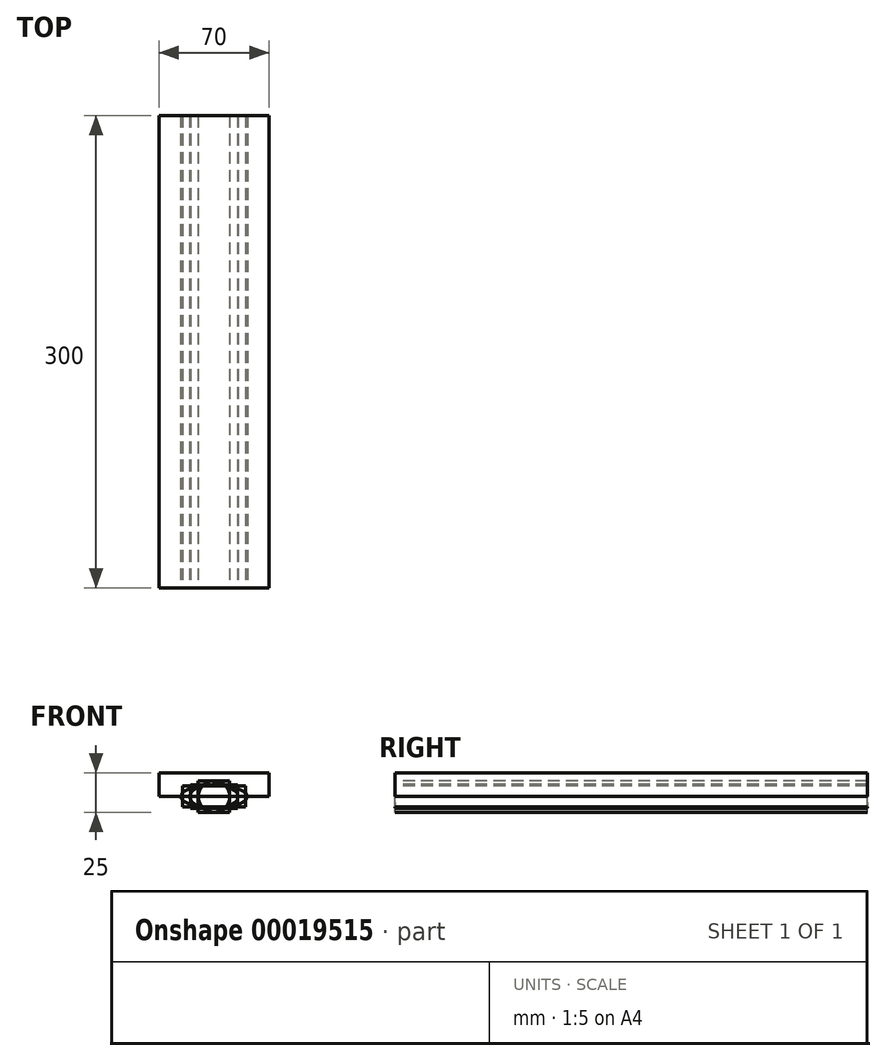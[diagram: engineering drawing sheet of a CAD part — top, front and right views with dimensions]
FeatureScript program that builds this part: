
annotation { "Feature Type Name" : "Feature", "Feature Type Description" : "" }
export const myFeature = defineFeature(function(context is Context, id is Id, definition is map)
    precondition{}
    {
        {
            var Q0;
            Q0=qCreatedBy(makeId("Front.planeOp"),FACE);
            var sketch = newSketch(context, id + "F0", { "sketchPlane" : qUnion([Q0])});
            skCircle(sketch, "E0", {"center": v(0, 0) * mm, "radius": 10 * mm});
            skSolve(sketch);
        }
        {
            var Q0;
            Q0=makeQuery(id+"F0.imprint","IMPRINT",FACE,{"disambiguationData":[TD([[makeQuery(id+"F0.imprint","IMPRINT",EDGE,{"derivedFrom":sQuery(id+"F0.wireOp",EDGE,"E0")}),1.0]])]});
            extrude(context, id + "F1", {"entities" : qUnion([Q0]), "oppositeDirection" : true, "depth" : (15 * 20) * mm});
        }
        {
            var Q0;
            Q0=qCreatedBy(makeId("Front.planeOp"),FACE);
            var sketch = newSketch(context, id + "F2", { "sketchPlane" : qUnion([Q0])});
            skLineSegment(sketch, "E1.bottom", {"start": v(10, 10) * mm, "end": v(-10, 10) * mm});
            skLineSegment(sketch, "E1.top", {"start": v(10, -10) * mm, "end": v(-10, -10) * mm});
            skLineSegment(sketch, "E1.left", {"start": v(10, 10) * mm, "end": v(10, -10) * mm});
            skLineSegment(sketch, "E1.right", {"start": v(-10, 10) * mm, "end": v(-10, -10) * mm});
            skPoint(sketch, "E1.middle", {"position": v(0, 0) * mm});
            skSolve(sketch);
        }
        {
            var Q0;
            Q0=makeQuery(id+"F2.imprint","IMPRINT",FACE,{"disambiguationData":[TD([[makeQuery(id+"F2.imprint","IMPRINT",EDGE,{"derivedFrom":sQuery(id+"F2.wireOp",EDGE,"E1.bottom")}),1.0]])]});
            extrude(context, id + "F3", {"entities" : qUnion([Q0]), "oppositeDirection" : true, "depth" : (15 * 20) * mm});
        }
        {
            var Q0;
            Q0=qCreatedBy(makeId("Front.planeOp"),FACE);
            var sketch = newSketch(context, id + "F4", { "sketchPlane" : qUnion([Q0])});
            skLineSegment(sketch, "E2.bottom", {"start": v(15, 7.5) * mm, "end": v(-15, 7.5) * mm});
            skLineSegment(sketch, "E2.top", {"start": v(15, -7.5) * mm, "end": v(-15, -7.5) * mm});
            skLineSegment(sketch, "E2.left", {"start": v(15, 7.5) * mm, "end": v(15, -7.5) * mm});
            skLineSegment(sketch, "E2.right", {"start": v(-15, 7.5) * mm, "end": v(-15, -7.5) * mm});
            skPoint(sketch, "E2.middle", {"position": v(0, 0) * mm});
            skSolve(sketch);
        }
        {
            var Q0;
            Q0=makeQuery(id+"F4.imprint","IMPRINT",FACE,{"disambiguationData":[TD([[makeQuery(id+"F4.imprint","IMPRINT",EDGE,{"derivedFrom":sQuery(id+"F4.wireOp",EDGE,"E2.bottom")}),1.0]])]});
            extrude(context, id + "F5", {"entities" : qUnion([Q0]), "oppositeDirection" : true, "depth" : (20 * 15) * mm});
        }
        {
            var Q0;
            Q0=qCreatedBy(makeId("Front.planeOp"),FACE);
            var sketch = newSketch(context, id + "F6", { "sketchPlane" : qUnion([Q0])});
            skEllipse(sketch, "E3", {"center": v(0, 0) * mm, "majorRadius": 15.42 * mm, "minorRadius": 7.7 * mm, "majorAxis": v(1, 0)});
            skSolve(sketch);
        }
        {
            var Q0;
            Q0=makeQuery(id+"F6.imprint","IMPRINT",FACE,{"disambiguationData":[TD([[makeQuery(id+"F6.imprint","IMPRINT",EDGE,{"derivedFrom":sQuery(id+"F6.wireOp",EDGE,"E3")}),1.0]])]});
            extrude(context, id + "F7", {"entities" : qUnion([Q0]), "oppositeDirection" : true, "depth" : (20 * 15) * mm});
        }
        {
            var Q0;
            Q0=qCreatedBy(makeId("Front.planeOp"),FACE);
            var sketch = newSketch(context, id + "F8", { "sketchPlane" : qUnion([Q0])});
            skLineSegment(sketch, "E4.bottom", {"start": v(20, 6.67) * mm, "end": v(-20, 6.67) * mm});
            skLineSegment(sketch, "E4.top", {"start": v(20, -6.67) * mm, "end": v(-20, -6.67) * mm});
            skLineSegment(sketch, "E4.left", {"start": v(20, 6.67) * mm, "end": v(20, -6.67) * mm});
            skLineSegment(sketch, "E4.right", {"start": v(-20, 6.67) * mm, "end": v(-20, -6.67) * mm});
            skPoint(sketch, "E4.middle", {"position": v(0, 0) * mm});
            skSolve(sketch);
        }
        {
            var Q0;
            Q0=makeQuery(id+"F8.imprint","IMPRINT",FACE,{"disambiguationData":[TD([[makeQuery(id+"F8.imprint","IMPRINT",EDGE,{"derivedFrom":sQuery(id+"F8.wireOp",EDGE,"E4.bottom")}),1.0]])]});
            extrude(context, id + "F9", {"entities" : qUnion([Q0]), "oppositeDirection" : true, "depth" : (20 * 15) * mm});
        }
        {
            var Q0;
            Q0=qCreatedBy(makeId("Front.planeOp"),FACE);
            var sketch = newSketch(context, id + "F10", { "sketchPlane" : qUnion([Q0])});
            skEllipse(sketch, "E5", {"center": v(0, 0) * mm, "majorRadius": 21.27 * mm, "minorRadius": 7.1 * mm, "majorAxis": v(1, 0)});
            skSolve(sketch);
        }
        {
            var Q0;
            Q0=makeQuery(id+"F10.imprint","IMPRINT",FACE,{"disambiguationData":[TD([[makeQuery(id+"F10.imprint","IMPRINT",EDGE,{"derivedFrom":sQuery(id+"F10.wireOp",EDGE,"E5")}),1.0]])]});
            extrude(context, id + "F11", {"entities" : qUnion([Q0]), "oppositeDirection" : true, "depth" : (20 * 15) * mm});
        }
        {
            var Q0;
            Q0=qCreatedBy(makeId("Front.planeOp"),FACE);
            var sketch = newSketch(context, id + "F12", { "sketchPlane" : qUnion([Q0])});
            skLineSegment(sketch, "E6.bottom", {"start": v(44.45, 44.45) * mm, "end": v(-44.45, 44.45) * mm});
            skLineSegment(sketch, "E6.top", {"start": v(44.45, -44.45) * mm, "end": v(-44.45, -44.45) * mm});
            skLineSegment(sketch, "E6.left", {"start": v(44.45, 44.45) * mm, "end": v(44.45, -44.45) * mm});
            skLineSegment(sketch, "E6.right", {"start": v(-44.45, 44.45) * mm, "end": v(-44.45, -44.45) * mm});
            skPoint(sketch, "E6.middle", {"position": v(0, 0) * mm});
            skSolve(sketch);
        }
        {
            var Q0;
            Q0=qCreatedBy(makeId("Right.planeOp"),FACE);
            var sketch = newSketch(context, id + "F13", { "sketchPlane" : qUnion([Q0])});
            skLineSegment(sketch, "E7", {"start": v(0, 0) * mm, "end": v(88.9, 0) * mm});
            skArc(sketch, "E8", {"start": v(88.9, 0) * mm, "mid": v(387.34, -298.44) * mm, "end": v(88.9, -596.87) * mm});
            skSolve(sketch);
        }
        {
            var Q0;
            Q0=makeQuery(id+"F12.imprint","IMPRINT",FACE,{"disambiguationData":[TD([[makeQuery(id+"F12.imprint","IMPRINT",EDGE,{"derivedFrom":sQuery(id+"F12.wireOp",EDGE,"E6.bottom")}),1.0]])]});
            var Q1;
            Q1=sQuery(id+"F13.wireOp",EDGE,"E7");
            var Q2;
            Q2=sQuery(id+"F13.wireOp",EDGE,"E8");
            sweep(context, id + "F14", {"profiles" : qUnion([Q0]), "path" : qUnion([Q1, Q2])});
        }
        {
            var Q0;
            Q0=makeQuery(id+"F14.opSweep","SWEPT_BODY",BODY,{"disambiguationData":[OSD([sQuery(id+"F12.wireOp",EDGE,"E6.bottom"),sQuery(id+"F12.wireOp",EDGE,"E6.top"),sQuery(id+"F12.wireOp",EDGE,"E6.left"),sQuery(id+"F12.wireOp",EDGE,"E6.right"),sQuery(id+"F13.wireOp",EDGE,"E8")])]});
            deleteBodies(context, id + "F15", {"entities" : qUnion([Q0])});
        }
        {
            var Q0;
            Q0=qCreatedBy(makeId("Front.planeOp"),FACE);
            var sketch = newSketch(context, id + "F16", { "sketchPlane" : qUnion([Q0])});
            skLineSegment(sketch, "E9.bottom", {"start": v(-35, 0) * mm, "end": v(35, 0) * mm});
            skLineSegment(sketch, "E9.top", {"start": v(-35, 15) * mm, "end": v(35, 15) * mm});
            skLineSegment(sketch, "E9.left", {"start": v(-35, 0) * mm, "end": v(-35, 15) * mm});
            skLineSegment(sketch, "E9.right", {"start": v(35, 0) * mm, "end": v(35, 15) * mm});
            skSolve(sketch);
        }
        {
            var Q0;
            Q0=makeQuery(id+"F16.imprint","IMPRINT",FACE,{"disambiguationData":[TD([[makeQuery(id+"F16.imprint","IMPRINT",EDGE,{"derivedFrom":sQuery(id+"F16.wireOp",EDGE,"E9.bottom")}),1.0]])]});
            extrude(context, id + "F17", {"entities" : qUnion([Q0]), "oppositeDirection" : true, "depth" : 300 * mm});
        }
    });
